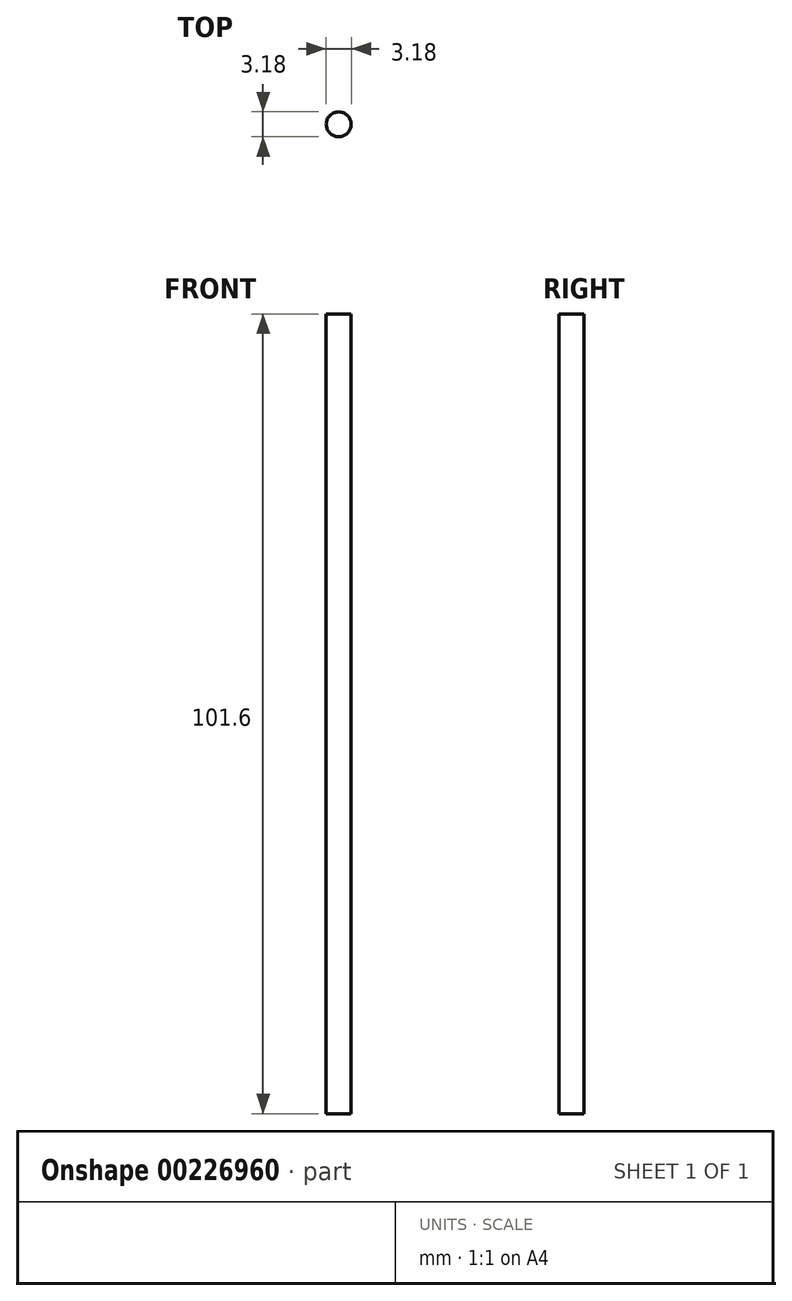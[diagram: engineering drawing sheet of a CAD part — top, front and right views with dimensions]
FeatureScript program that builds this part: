
annotation { "Feature Type Name" : "Feature", "Feature Type Description" : "" }
export const myFeature = defineFeature(function(context is Context, id is Id, definition is map)
    precondition{}
    {
        {
            var Q0;
            Q0=qCreatedBy(makeId("Top.planeOp"),FACE);
            var sketch = newSketch(context, id + "F0", { "sketchPlane" : qUnion([Q0])});
            skCircle(sketch, "E0", {"center": v(-45.9, 48.72) * mm, "radius": 1.59 * mm});
            skSolve(sketch);
        }
        {
            var Q0;
            Q0 = qSketchRegion(id + "F0", true);
            extrude(context, id + "F1", {"entities" : qUnion([Q0]), "depth" : 101.6 * mm});
        }
    });
